FCSTD DOCUMENT  (FreeCAD 0.19R)
Label: GT2_Profil
License: All rights reserved
LicenseURL: http://en.wikipedia.org/wiki/All_rights_reserved
objects: Sketcher::SketchObject×1, PartDesign::Body×1
note: 2 computed .brp shape members not serialized (recipe doc carries the construction recipe); baked Part::Feature solids carry a one-line shape summary decoded from their .brp

FEATURE [Sketcher::SketchObject] Sketch
  MapMode = 5
  Support = -> [XY_Plane]
  sketch-geometry (29):
    g0: LineSegment StartX=-53.5076 StartY=0 StartZ=0 EndX=68.7323 EndY=0 EndZ=0
    g1: LineSegment [constr] StartX=-44.4816 StartY=-1.38 StartZ=0 EndX=7.22751 EndY=-1.38 EndZ=0
    g2: LineSegment [constr] StartX=-12.3003 StartY=-0.63 StartZ=0 EndX=7.21073 EndY=-0.63 EndZ=0
    g3: ArcOfCircle CenterX=0.4 CenterY=-0.63 CenterZ=0 NormalX=0 NormalY=0 NormalZ=1 AngleXU=0 Radius=0.997214 StartAngle=3.27272 EndAngle=3.60524
    g4: ArcOfCircle CenterX=0 CenterY=-0.83 CenterZ=0 NormalX=0 NormalY=0 NormalZ=1 AngleXU=0 Radius=0.55 StartAngle=3.60524 EndAngle=5.88755
    g5: ArcOfCircle CenterX=-2 CenterY=-0.83 CenterZ=0 NormalX=0 NormalY=0 NormalZ=1 AngleXU=0 Radius=0.55 StartAngle=3.60524 EndAngle=5.81954
    g6: ArcOfCircle CenterX=-1.6 CenterY=-0.63 CenterZ=0 NormalX=0 NormalY=0 NormalZ=1 AngleXU=0 Radius=0.997214 StartAngle=3.27272 EndAngle=3.60524
    g7: LineSegment StartX=-1.26264 StartY=-0.63 StartZ=0 EndX=-0.737365 EndY=-0.63 EndZ=0
    g8: ArcOfCircle CenterX=-0.737365 CenterY=-0.78 CenterZ=0 NormalX=0 NormalY=0 NormalZ=1 AngleXU=0 Radius=0.15 StartAngle=0.131127 EndAngle=1.5708
    g9: ArcOfCircle CenterX=-2.4 CenterY=-0.63 CenterZ=0 NormalX=0 NormalY=0 NormalZ=1 AngleXU=0 Radius=0.997214 StartAngle=5.81954 EndAngle=6.15206
    g10: ArcOfCircle CenterX=-1.26264 CenterY=-0.78 CenterZ=0 NormalX=0 NormalY=0 NormalZ=1 AngleXU=0 Radius=0.15 StartAngle=1.5708 EndAngle=3.01047
    g11: ArcOfCircle CenterX=-4 CenterY=-0.83 CenterZ=0 NormalX=0 NormalY=0 NormalZ=1 AngleXU=0 Radius=0.55 StartAngle=3.60524 EndAngle=5.81954
    g12: LineSegment StartX=-3.26264 StartY=-0.63 StartZ=0 EndX=-2.73736 EndY=-0.63 EndZ=0
    g13: ArcOfCircle CenterX=-2.73736 CenterY=-0.78 CenterZ=0 NormalX=0 NormalY=0 NormalZ=1 AngleXU=0 Radius=0.15 StartAngle=0.131127 EndAngle=1.5708
    g14: ArcOfCircle CenterX=-4.4 CenterY=-0.63 CenterZ=0 NormalX=0 NormalY=0 NormalZ=1 AngleXU=0 Radius=0.997214 StartAngle=5.81954 EndAngle=6.15206
    g15: ArcOfCircle CenterX=-3.26264 CenterY=-0.78 CenterZ=0 NormalX=0 NormalY=0 NormalZ=1 AngleXU=0 Radius=0.15 StartAngle=1.5708 EndAngle=3.01047
    g16: ArcOfCircle CenterX=-3.6 CenterY=-0.63 CenterZ=0 NormalX=0 NormalY=0 NormalZ=1 AngleXU=0 Radius=0.997214 StartAngle=3.27272 EndAngle=3.60524
    g17: ArcOfCircle CenterX=-6 CenterY=-0.83 CenterZ=0 NormalX=0 NormalY=0 NormalZ=1 AngleXU=0 Radius=0.55 StartAngle=3.60524 EndAngle=5.81954
    g18: ArcOfCircle CenterX=-5.6 CenterY=-0.63 CenterZ=0 NormalX=0 NormalY=0 NormalZ=1 AngleXU=0 Radius=0.997214 StartAngle=3.27272 EndAngle=3.60524
    g19: LineSegment StartX=-5.26264 StartY=-0.63 StartZ=0 EndX=-4.73736 EndY=-0.63 EndZ=0
    g20: ArcOfCircle CenterX=-4.73736 CenterY=-0.78 CenterZ=0 NormalX=0 NormalY=0 NormalZ=1 AngleXU=0 Radius=0.15 StartAngle=0.131127 EndAngle=1.5708
    g21: ArcOfCircle CenterX=-6.4 CenterY=-0.63 CenterZ=0 NormalX=0 NormalY=0 NormalZ=1 AngleXU=0 Radius=0.997214 StartAngle=5.81954 EndAngle=6.15206
    g22: ArcOfCircle CenterX=-5.26264 CenterY=-0.78 CenterZ=0 NormalX=0 NormalY=0 NormalZ=1 AngleXU=0 Radius=0.15 StartAngle=1.5708 EndAngle=3.01047
    g23: ArcOfCircle CenterX=-8 CenterY=-0.83 CenterZ=0 NormalX=0 NormalY=0 NormalZ=1 AngleXU=0 Radius=0.55 StartAngle=3.31732 EndAngle=5.81954
    g24: ArcOfCircle CenterX=-7.6 CenterY=-0.758976 CenterZ=0 NormalX=0 NormalY=0 NormalZ=1 AngleXU=0 Radius=0.956257 StartAngle=3.26942 EndAngle=3.31732
    g25: LineSegment StartX=-7.26264 StartY=-0.63 StartZ=0 EndX=-6.73736 EndY=-0.63 EndZ=0
    g26: ArcOfCircle CenterX=-6.73736 CenterY=-0.78 CenterZ=0 NormalX=0 NormalY=0 NormalZ=1 AngleXU=0 Radius=0.15 StartAngle=0.131127 EndAngle=1.5708
    g27: ArcOfCircle CenterX=-8.4 CenterY=-0.63 CenterZ=0 NormalX=0 NormalY=0 NormalZ=1 AngleXU=0 Radius=0.997214 StartAngle=5.81954 EndAngle=6.15206
    g28: ArcOfCircle CenterX=-7.26264 CenterY=-0.78 CenterZ=0 NormalX=0 NormalY=0 NormalZ=1 AngleXU=0 Radius=0.15 StartAngle=1.5708 EndAngle=3.01047
  constraints (79):
    c: PointOnObject(g0,g-1)
    c: PointOnObject(g0,g-1)
    c: Horizontal(g1)
    c: DistanceY(g1,g0) = 1.38
    c: Horizontal(g2)
    c: DistanceY(g1,g2) = 0.75
    c: PointOnObject(g3,g2)
    c: PointOnObject(g4,g-2)
    c: Tangent(g4,g1)
    c: Radius(g4) = 0.55
    c: DistanceX(g3) = 0.4
    c: Tangent(g4,g3) = -1.5708
    c: Equal(g4,g5) = 0.55
    c: Tangent(g5,g6) = -1.5708
    c: DistanceX(g5,g4) = 2
    c: Tangent(g5,g1)
    c: PointOnObject(g7,g2)
    c: PointOnObject(g7,g2)
    c: Radius(g8) = 0.15
    c: Tangent(g8,g3) = 1.5708
    c: Tangent(g8,g7) = 1.5708
    c: Tangent(g10,g7) = 1.5708
    c: Tangent(g10,g9) = 1.5708
    c: Tangent(g9,g5) = -1.5708
    c: PointOnObject(g9,g2)
    c: DistanceX(g9,g5) = 0.4
    c: Equal(g8,g13) = 0.15
    c: Tangent(g13,g12) = 1.5708
    c: Tangent(g15,g12) = 1.5708
    c: Tangent(g15,g14) = 1.5708
    c: Tangent(g14,g11) = -1.5708
    c: DistanceX(g14,g11) = 0.4
    c: PointOnObject(g12,g2)
    c: PointOnObject(g12,g2)
    c: Tangent(g11,g1)
    c: DistanceX(g11,g5) = 2
    c: Equal(g5,g11)
    c: Equal(g13,g15)
    c: Equal(g10,g8)
    c: Tangent(g6,g13) = 1.5708
    c: DistanceX(g5,g6) = 0.4
    c: Equal(g6,g9)
    c: Equal(g6,g14)
    c: Tangent(g17,g18) = -1.5708
    c: Equal(g8,g20) = 0.15
    c: Tangent(g20,g16) = 1.5708
    c: Tangent(g20,g19) = 1.5708
    c: Tangent(g22,g19) = 1.5708
    c: Tangent(g22,g21) = 1.5708
    c: Tangent(g21,g17) = -1.5708
    c: DistanceX(g21,g17) = 0.4
    c: Tangent(g23,g24) = -1.5708
    c: Equal(g20,g26) = 0.15
    c: Tangent(g26,g25) = 1.5708
    c: Tangent(g28,g25) = 1.5708
    c: Tangent(g28,g27) = 1.5708
    c: Tangent(g27,g23) = -1.5708
    c: DistanceX(g27,g23) = 0.4
    c: DistanceX(g23,g17) = 2
    c: Equal(g17,g23)
    c: Equal(g26,g28)
    c: Equal(g22,g20)
    c: Tangent(g18,g26) = 1.5708
    c: DistanceX(g17,g18) = 0.4
    c: Equal(g18,g27)
    c: DistanceX(g17,g11) = 2
    c: PointOnObject(g19,g2)
    c: Tangent(g17,g1)
    c: Tangent(g23,g1)
    c: Tangent(g11,g16) = -1.5708
    c: PointOnObject(g25,g2)
    c: Horizontal(g19)
    c: Horizontal(g25)
    c: Equal(g21,g16)
    c: DistanceX(g11,g16) = 0.4
    c: DistanceX(g23,g24) = 0.4
    c: Equal(g16,g14)
    c: Equal(g21,g18)
    c: PointOnObject(g18,g2)
FEATURE [PartDesign::Body] Body
  Group = -> [Sketch]
  Origin = -> Origin
